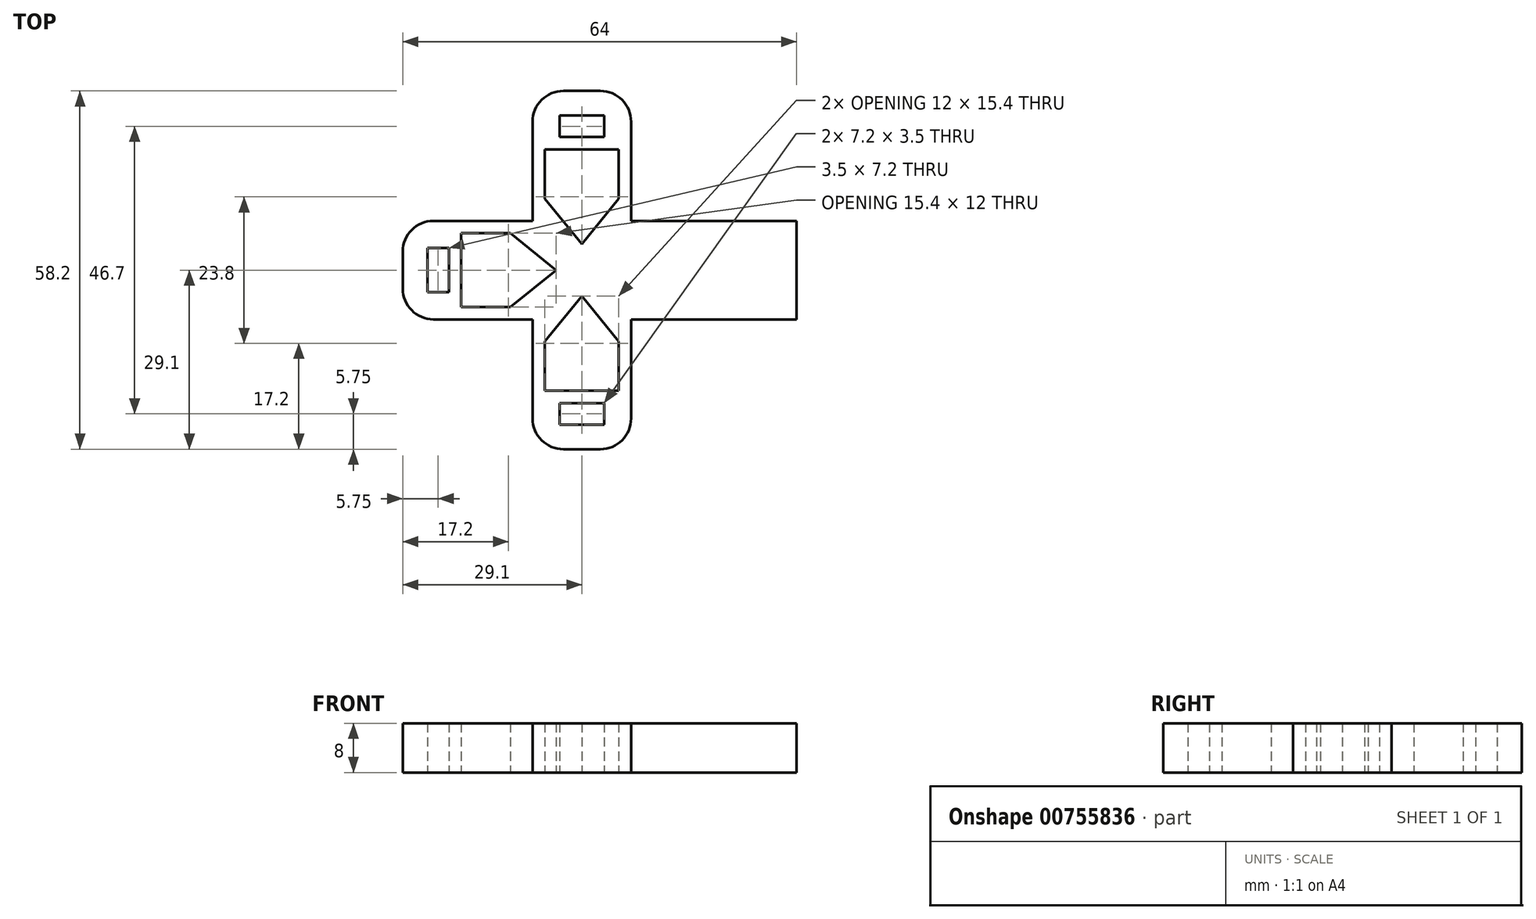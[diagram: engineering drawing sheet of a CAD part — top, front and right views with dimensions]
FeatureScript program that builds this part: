
annotation { "Feature Type Name" : "Feature", "Feature Type Description" : "" }
export const myFeature = defineFeature(function(context is Context, id is Id, definition is map)
    precondition{}
    {
        {
            var Q0;
            Q0=qCreatedBy(makeId("Top.planeOp"),FACE);
            var sketch = newSketch(context, id + "F0", { "sketchPlane" : qUnion([Q0])});
            skLineSegment(sketch, "E0.bottom", {"start": v(0, 0) * mm, "end": v(16.1, 0) * mm});
            skLineSegment(sketch, "E0.top", {"start": v(0, 16) * mm, "end": v(16.1, 16) * mm});
            skLineSegment(sketch, "E0.right", {"start": v(59, 0) * mm, "end": v(59, 16) * mm});
            skArc(sketch, "E1", {"start": v(0, 16) * mm, "mid": v(-3.54, 14.54) * mm, "end": v(-5, 11) * mm});
            skArc(sketch, "E2", {"start": v(-5, 5) * mm, "mid": v(-3.54, 1.46) * mm, "end": v(0, 0) * mm});
            skLineSegment(sketch, "E3.bottom", {"start": v(-1, 11.6) * mm, "end": v(2.5, 11.6) * mm});
            skLineSegment(sketch, "E3.top", {"start": v(-1, 4.4) * mm, "end": v(2.5, 4.4) * mm});
            skLineSegment(sketch, "E3.left", {"start": v(-1, 11.6) * mm, "end": v(-1, 4.4) * mm});
            skLineSegment(sketch, "E3.right", {"start": v(2.5, 11.6) * mm, "end": v(2.5, 4.4) * mm});
            skLineSegment(sketch, "E4.bottom", {"start": v(4.5, 2) * mm, "end": v(12.5, 2) * mm});
            skLineSegment(sketch, "E4.top", {"start": v(4.5, 14) * mm, "end": v(12.5, 14) * mm});
            skLineSegment(sketch, "E4.left", {"start": v(4.5, 2) * mm, "end": v(4.5, 14) * mm});
            skLineSegment(sketch, "E5", {"start": v(19.9, 8) * mm, "end": v(12.5, 14) * mm});
            skLineSegment(sketch, "E6", {"start": v(19.9, 8) * mm, "end": v(12.5, 2) * mm});
            skLineSegment(sketch, "E7", {"start": v(-5, 11) * mm, "end": v(-5, 5) * mm});
            skLineSegment(sketch, "E8.1.0", {"start": v(18.1, 27.6) * mm, "end": v(30.1, 27.6) * mm});
            skLineSegment(sketch, "E8.1.1", {"start": v(30.1, 27.6) * mm, "end": v(30.1, 19.6) * mm});
            skLineSegment(sketch, "E8.1.2", {"start": v(24.1, 12.2) * mm, "end": v(30.1, 19.6) * mm});
            skLineSegment(sketch, "E8.1.3", {"start": v(24.1, 12.2) * mm, "end": v(18.1, 19.6) * mm});
            skLineSegment(sketch, "E8.1.4", {"start": v(18.1, 27.6) * mm, "end": v(18.1, 19.6) * mm});
            skLineSegment(sketch, "E8.1.5", {"start": v(27.7, 29.6) * mm, "end": v(20.5, 29.6) * mm});
            skLineSegment(sketch, "E8.1.6", {"start": v(27.7, 33.1) * mm, "end": v(27.7, 29.6) * mm});
            skLineSegment(sketch, "E8.1.7", {"start": v(27.7, 33.1) * mm, "end": v(20.5, 33.1) * mm});
            skLineSegment(sketch, "E8.1.8", {"start": v(20.5, 33.1) * mm, "end": v(20.5, 29.6) * mm});
            skArc(sketch, "E8.1.9", {"start": v(32.1, 32.1) * mm, "mid": v(30.64, 35.64) * mm, "end": v(27.1, 37.1) * mm});
            skLineSegment(sketch, "E8.1.10", {"start": v(27.1, 37.1) * mm, "end": v(21.1, 37.1) * mm});
            skArc(sketch, "E8.1.11", {"start": v(21.1, 37.1) * mm, "mid": v(17.56, 35.64) * mm, "end": v(16.1, 32.1) * mm});
            skPoint(sketch, "E8.center", {"position": v(24.1, 8) * mm});
            skLineSegment(sketch, "E8.anchor1", {"start": v(24.1, 8) * mm, "end": v(19.9, 8) * mm, "construction": true});
            skLineSegment(sketch, "E8.anchor2", {"start": v(24.1, 8) * mm, "end": v(24.1, 12.2) * mm, "construction": true});
            skLineSegment(sketch, "E9.1.0", {"start": v(30.1, -11.6) * mm, "end": v(30.1, -3.6) * mm});
            skLineSegment(sketch, "E9.1.1", {"start": v(30.1, -11.6) * mm, "end": v(18.1, -11.6) * mm});
            skLineSegment(sketch, "E9.1.2", {"start": v(18.1, -11.6) * mm, "end": v(18.1, -3.6) * mm});
            skLineSegment(sketch, "E9.1.3", {"start": v(24.1, 3.8) * mm, "end": v(18.1, -3.6) * mm});
            skLineSegment(sketch, "E9.1.4", {"start": v(24.1, 3.8) * mm, "end": v(30.1, -3.6) * mm});
            skLineSegment(sketch, "E9.1.5", {"start": v(27.7, -17.1) * mm, "end": v(27.7, -13.6) * mm});
            skLineSegment(sketch, "E9.1.6", {"start": v(20.5, -17.1) * mm, "end": v(27.7, -17.1) * mm});
            skLineSegment(sketch, "E9.1.7", {"start": v(20.5, -13.6) * mm, "end": v(27.7, -13.6) * mm});
            skLineSegment(sketch, "E9.1.8", {"start": v(20.5, -17.1) * mm, "end": v(20.5, -13.6) * mm});
            skArc(sketch, "E9.1.9", {"start": v(16.1, -16.1) * mm, "mid": v(17.56, -19.64) * mm, "end": v(21.1, -21.1) * mm});
            skLineSegment(sketch, "E9.1.10", {"start": v(21.1, -21.1) * mm, "end": v(27.1, -21.1) * mm});
            skArc(sketch, "E9.1.11", {"start": v(27.1, -21.1) * mm, "mid": v(30.64, -19.64) * mm, "end": v(32.1, -16.1) * mm});
            skLineSegment(sketch, "E10", {"start": v(16.1, 32.1) * mm, "end": v(16.1, 16) * mm});
            skLineSegment(sketch, "E11", {"start": v(32.1, 32.1) * mm, "end": v(32.1, 16) * mm});
            skLineSegment(sketch, "E12", {"start": v(16.1, -16.1) * mm, "end": v(16.1, 0) * mm});
            skLineSegment(sketch, "E13", {"start": v(32.1, -16.1) * mm, "end": v(32.1, 0) * mm});
            skLineSegment(sketch, "E14.trimOffspring", {"start": v(32.1, 16) * mm, "end": v(59, 16) * mm});
            skLineSegment(sketch, "E15.trimOffspring", {"start": v(32.1, 0) * mm, "end": v(59, 0) * mm});
            skSolve(sketch);
        }
        {
            var Q0;
            Q0=makeQuery(id+"F0.imprint","IMPRINT",FACE,{"disambiguationData":[TD([[makeQuery(id+"F0.imprint","IMPRINT",EDGE,{"derivedFrom":sQuery(id+"F0.wireOp",EDGE,"E0.bottom")}),1.0]])]});
            extrude(context, id + "F1", {"entities" : qUnion([Q0]), "depth" : 8 * mm, "offsetDistance" : 25 * mm});
        }
    });
